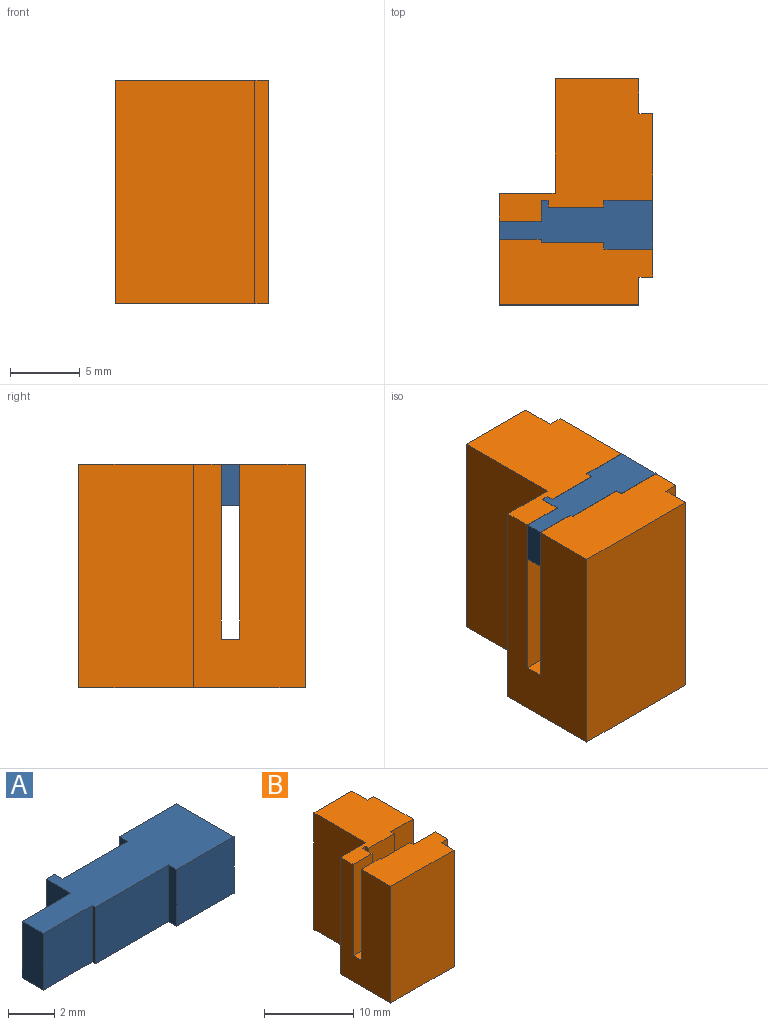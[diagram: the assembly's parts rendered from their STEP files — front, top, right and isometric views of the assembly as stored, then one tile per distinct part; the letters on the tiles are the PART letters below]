
ASSEMBLY  parts=2 mates=1
PART A: 16 faces, bbox 11x3.5x3 mm
  f0: plane 3.5x3mm, normal (0,-1,0), area 10.5mm2, adj f1,f13,f14,f15
  f1: plane 3.5x3mm, normal (1,0,0), area 10.5mm2, adj f0,f2,f14,f15
  f2: plane 3.5x3mm, normal (0,1,0), area 10.5mm2, adj f1,f3,f14,f15
  f3: plane 3x0.5mm, normal (-1,0,0), area 1.5mm2, adj f2,f4,f14,f15
  f4: plane 4x3mm, normal (0,1,0), area 12mm2, adj f3,f5,f14,f15
  f5: plane 3x0.5mm, normal (1,0,0), area 1.5mm2, adj f4,f6,f14,f15
  f6: plane 3x0.5mm, normal (0,1,0), area 1.5mm2, adj f5,f7,f14,f15
  f7: plane 3x1.5mm, normal (-1,0,0), area 4.5mm2, adj f6,f8,f14,f15
  f8: plane 3x3mm, normal (0,1,0), area 9mm2, adj f7,f9,f14,f15
  f9: plane 3x1.3mm, normal (-1,0,0), area 3.9mm2, adj f8,f10,f14,f15
  f10: plane 3x3mm, normal (0,-1,0), area 9mm2, adj f9,f11,f14,f15
  f11: plane 3x0.2mm, normal (-1,0,0), area 0.6mm2, adj f10,f12,f14,f15
  f12: plane 4.5x3mm, normal (0,-1,0), area 13.5mm2, adj f11,f13,f14,f15
  f13: plane 3x0.5mm, normal (-1,0,0), area 1.5mm2, adj f0,f12,f14,f15
  f14: plane 11x3.5mm, normal (0,0,1), area 27.7mm2, adj f0,f1,f2,f3,f4,f5,f6,f7
  f15: plane 11x3.5mm, normal (0,0,-1), area 27.7mm2, adj f0,f1,f2,f3,f4,f5,f6,f7
PART B: 26 faces, bbox 11x16.2x16 mm
  f0: plane 12.5x3mm, normal (0,1,0), area 37.5mm2, adj f1,f9,f10,f25
  f1: plane 16x8mm, normal (-1,0,0), area 111.7mm2, adj f0,f2,f10,f11,f12,f13,f24,f25
  f2: plane 16x10mm, normal (0,-1,0), area 160mm2, adj f1,f3,f10,f11
  f3: plane 16x2mm, normal (1,0,0), area 32mm2, adj f2,f4,f10,f11
  f4: plane 16x1mm, normal (0,-1,0), area 16mm2, adj f3,f5,f10,f11
  f5: plane 16x11.7mm, normal (1,0,0), area 143.4mm2, adj f4,f6,f10,f11,f19,f20,f24,f25
  f6: plane 12.5x3.5mm, normal (0,1,0), area 43.8mm2, adj f5,f7,f10,f25
  f7: plane 12.5x0.5mm, normal (1,0,0), area 6.3mm2, adj f6,f8,f10,f25
  f8: plane 12.5x4.5mm, normal (0,1,0), area 56.2mm2, adj f7,f9,f10,f25
  f9: plane 12.5x0.2mm, normal (1,0,0), area 2.5mm2, adj f0,f8,f10,f25
  f10: plane 11x4.7mm, normal (0,0,1), area 46.3mm2, adj f0,f1,f2,f3,f4,f5,f6,f7
  f11: plane 16.2x11mm, normal (0,0,-1), area 140.9mm2, adj f1,f2,f3,f4,f5,f12,f20,f21
  f12: plane 16x4mm, normal (0,1,0), area 64mm2, adj f1,f11,f23,f24
  f13: plane 12.5x3mm, normal (0,-1,0), area 37.5mm2, adj f1,f14,f24,f25
  f14: plane 12.5x1.5mm, normal (1,0,0), area 18.8mm2, adj f13,f15,f24,f25
  f15: plane 12.5x0.5mm, normal (0,-1,0), area 6.3mm2, adj f14,f16,f24,f25
  f16: plane 12.5x0.5mm, normal (-1,0,0), area 6.3mm2, adj f15,f17,f24,f25
  f17: plane 12.5x4mm, normal (0,-1,0), area 50mm2, adj f16,f18,f24,f25
  f18: plane 12.5x0.5mm, normal (1,0,0), area 6.3mm2, adj f17,f19,f24,f25
  f19: plane 12.5x3.5mm, normal (0,-1,0), area 43.8mm2, adj f5,f18,f24,f25
  f20: plane 16x1mm, normal (0,1,0), area 16mm2, adj f5,f11,f21,f24
  f21: plane 16x2.5mm, normal (1,0,0), area 40mm2, adj f11,f20,f22,f24
  f22: plane 16x6mm, normal (0,1,0), area 96mm2, adj f11,f21,f23,f24
  f23: plane 16x8.2mm, normal (-1,0,0), area 131.2mm2, adj f11,f12,f22,f24
  f24: plane 11x10.2mm, normal (0,0,1), area 66.9mm2, adj f1,f5,f12,f13,f14,f15,f16,f17
  f25: plane 11x3.5mm, normal (0,0,1), area 27.7mm2, adj f0,f1,f5,f6,f7,f8,f9,f13
PLACE A t=(27.55,-40.35,3.36)mm
PLACE B t=(28.53,-38.8,-9.67)mm fixed
MATE slider B.f25 <-> A.f14  axis (0,0,1) through (-3.95,-4.27,-6.17)mm
